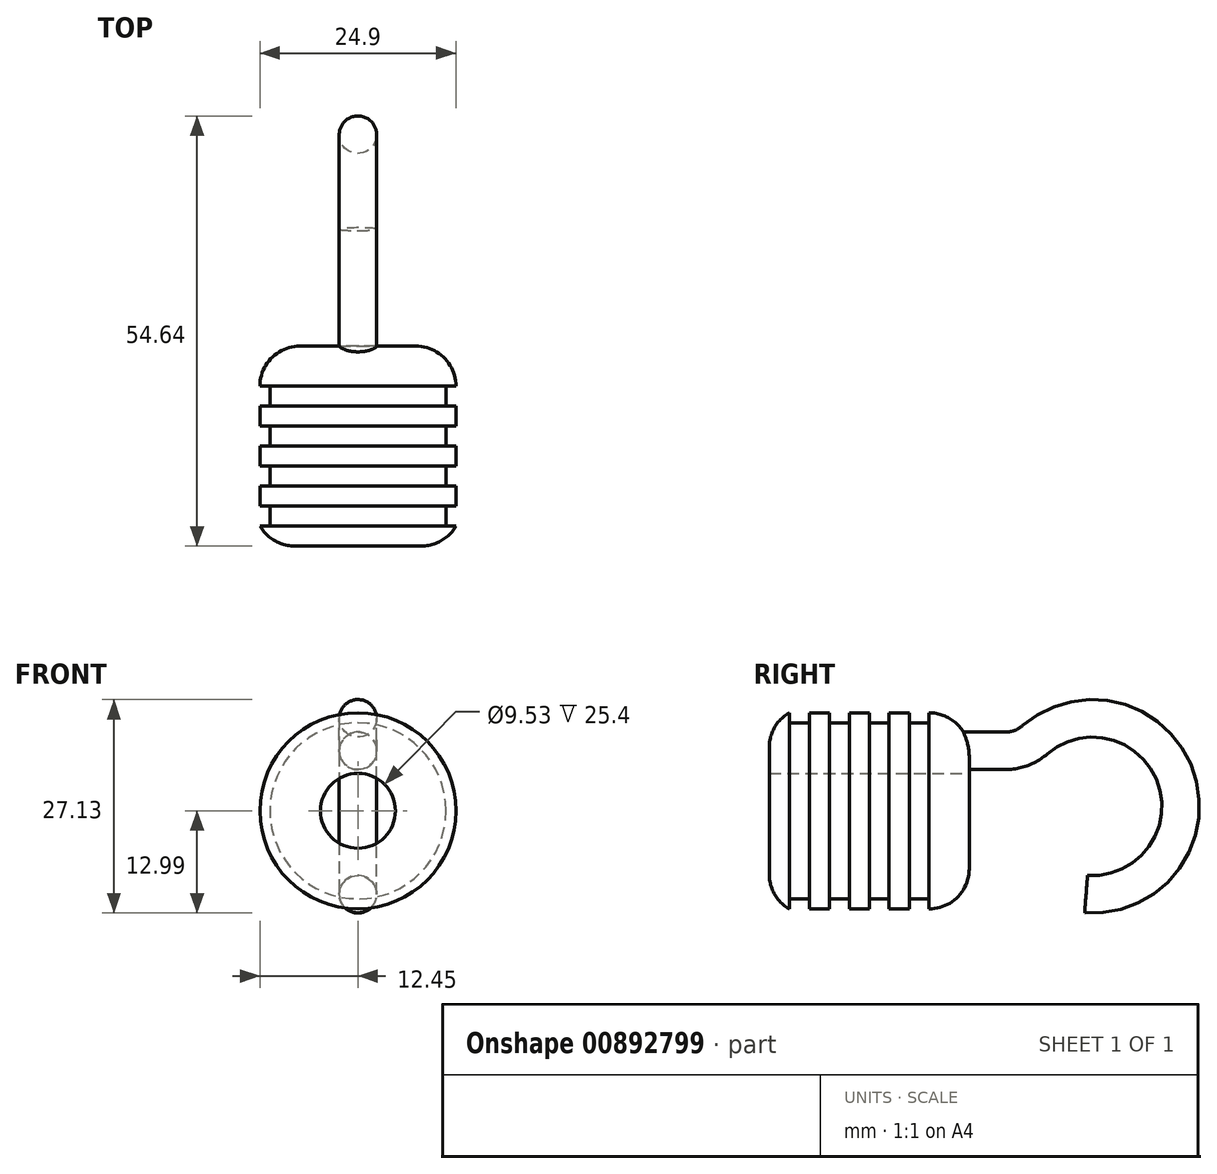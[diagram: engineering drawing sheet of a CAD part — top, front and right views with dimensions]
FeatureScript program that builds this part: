
annotation { "Feature Type Name" : "Feature", "Feature Type Description" : "" }
export const myFeature = defineFeature(function(context is Context, id is Id, definition is map)
    precondition{}
    {
        {
            var Q0;
            Q0=qCreatedBy(makeId("Right.planeOp"),FACE);
            var sketch = newSketch(context, id + "F0", { "sketchPlane" : qUnion([Q0])});
            skLineSegment(sketch, "E0", {"start": v(1.3, 4.76) * mm, "end": v(26.7, 4.76) * mm});
            skLineSegment(sketch, "E1", {"start": v(26.7, 12.45) * mm, "end": v(21.62, 12.45) * mm});
            skLineSegment(sketch, "E2", {"start": v(21.62, 12.45) * mm, "end": v(21.62, 11.18) * mm});
            skLineSegment(sketch, "E3", {"start": v(21.62, 11.18) * mm, "end": v(19.08, 11.18) * mm});
            skLineSegment(sketch, "E4", {"start": v(19.08, 11.18) * mm, "end": v(19.08, 12.45) * mm});
            skLineSegment(sketch, "E5", {"start": v(19.08, 12.45) * mm, "end": v(16.54, 12.45) * mm});
            skLineSegment(sketch, "E6", {"start": v(16.54, 12.45) * mm, "end": v(16.54, 11.18) * mm});
            skLineSegment(sketch, "E7", {"start": v(16.54, 11.18) * mm, "end": v(14, 11.18) * mm});
            skLineSegment(sketch, "E8", {"start": v(14, 11.18) * mm, "end": v(14, 12.45) * mm});
            skLineSegment(sketch, "E9", {"start": v(14, 12.45) * mm, "end": v(11.46, 12.45) * mm});
            skLineSegment(sketch, "E10", {"start": v(11.46, 12.45) * mm, "end": v(11.46, 11.18) * mm});
            skLineSegment(sketch, "E11", {"start": v(11.46, 11.18) * mm, "end": v(8.92, 11.18) * mm});
            skLineSegment(sketch, "E12", {"start": v(8.92, 11.18) * mm, "end": v(8.92, 12.45) * mm});
            skLineSegment(sketch, "E13", {"start": v(8.92, 12.45) * mm, "end": v(6.38, 12.45) * mm});
            skLineSegment(sketch, "E14", {"start": v(6.38, 12.45) * mm, "end": v(6.38, 11.18) * mm});
            skLineSegment(sketch, "E15", {"start": v(6.38, 11.18) * mm, "end": v(3.84, 11.18) * mm});
            skLineSegment(sketch, "E16", {"start": v(3.84, 11.18) * mm, "end": v(3.84, 12.45) * mm});
            skLineSegment(sketch, "E17", {"start": v(3.84, 12.45) * mm, "end": v(1.3, 12.45) * mm});
            skLineSegment(sketch, "E18", {"start": v(1.3, 12.45) * mm, "end": v(1.3, 4.76) * mm});
            skLineSegment(sketch, "E19", {"start": v(26.7, 12.45) * mm, "end": v(26.7, 4.76) * mm});
            skLineSegment(sketch, "E20", {"start": v(31.69, 0) * mm, "end": v(-2.34, 0) * mm, "construction": true});
            skSolve(sketch);
        }
        {
            var Q0;
            Q0=makeQuery(id+"F0.imprint","IMPRINT",FACE,{"disambiguationData":[TD([[makeQuery(id+"F0.imprint","IMPRINT",EDGE,{"derivedFrom":sQuery(id+"F0.wireOp",EDGE,"E0")}),1.0]])]});
            var Q1;
            Q1=sQuery(id+"F0.wireOp",EDGE,"E20");
            revolve(context, id + "F1", {"surfaceOperationType" : NewSurfaceOperationType.NEW, "entities" : qUnion([Q0]), "axis" : qUnion([Q1]), "revolveType" : RevolveType.FULL});
        }
        {
            var Q0;
            Q0=makeQuery(id+"F1.opRevolve","SWEPT_FACE",FACE,{"disambiguationData":[OSD([sQuery(id+"F0.wireOp",EDGE,"E19")])]});
            var sketch = newSketch(context, id + "F2", { "sketchPlane" : qUnion([Q0])});
            skCircle(sketch, "E21", {"center": v(0, 7.62) * mm, "radius": 2.38 * mm});
            skSolve(sketch);
        }
        {
            var Q0;
            Q0=qCreatedBy(makeId("Right.planeOp"),FACE);
            var sketch = newSketch(context, id + "F3", { "sketchPlane" : qUnion([Q0])});
            skLineSegment(sketch, "E22", {"start": v(26.7, 6.99) * mm, "end": v(31.3, 6.99) * mm});
            skArc(sketch, "E23", {"start": v(41.6, -9.94) * mm, "mid": v(52.39, 3.9) * mm, "end": v(35.46, 8.54) * mm});
            skPoint(sketch, "E24.visualSharp", {"position": v(34, 6.99) * mm});
            skArc(sketch, "E24.filletArc", {"start": v(31.3, 6.99) * mm, "mid": v(33.52, 7.39) * mm, "end": v(35.46, 8.54) * mm});
            skSolve(sketch);
        }
        {
            var Q0;
            Q0=makeQuery(id+"F2.imprint","IMPRINT",FACE,{"disambiguationData":[TD([[makeQuery(id+"F2.imprint","IMPRINT",EDGE,{"derivedFrom":sQuery(id+"F2.wireOp",EDGE,"E21")}),1.0]])]});
            var Q1;
            Q1=sQuery(id+"F3.wireOp",EDGE,"E23");
            var Q2;
            Q2=sQuery(id+"F3.wireOp",EDGE,"E24.filletArc");
            var Q3;
            Q3=sQuery(id+"F3.wireOp",EDGE,"E22");
            sweep(context, id + "F4", {"operationType" : NewBodyOperationType.ADD, "profiles" : qUnion([Q0]), "path" : qUnion([Q1, Q2, Q3])});
        }
        {
            var Q0;
            Q0=makeQuery(id+"F1.opRevolve","SWEPT_EDGE",EDGE,{"disambiguationData":[OSD([sQuery(id+"F0.wireOp",EDGE,"E1"),sQuery(id+"F0.wireOp",EDGE,"E19")])]});
            var Q1;
            Q1=makeQuery(id+"F1.opRevolve","SWEPT_EDGE",EDGE,{"disambiguationData":[OSD([sQuery(id+"F0.wireOp",EDGE,"E17"),sQuery(id+"F0.wireOp",EDGE,"E18")])]});
            fillet(context, id + "F5", {"entities" : qUnion([Q0, Q1]), "radius" : 5.08 * mm, "tangentPropagation" : true, "allowEdgeOverflow" : false});
        }
    });
